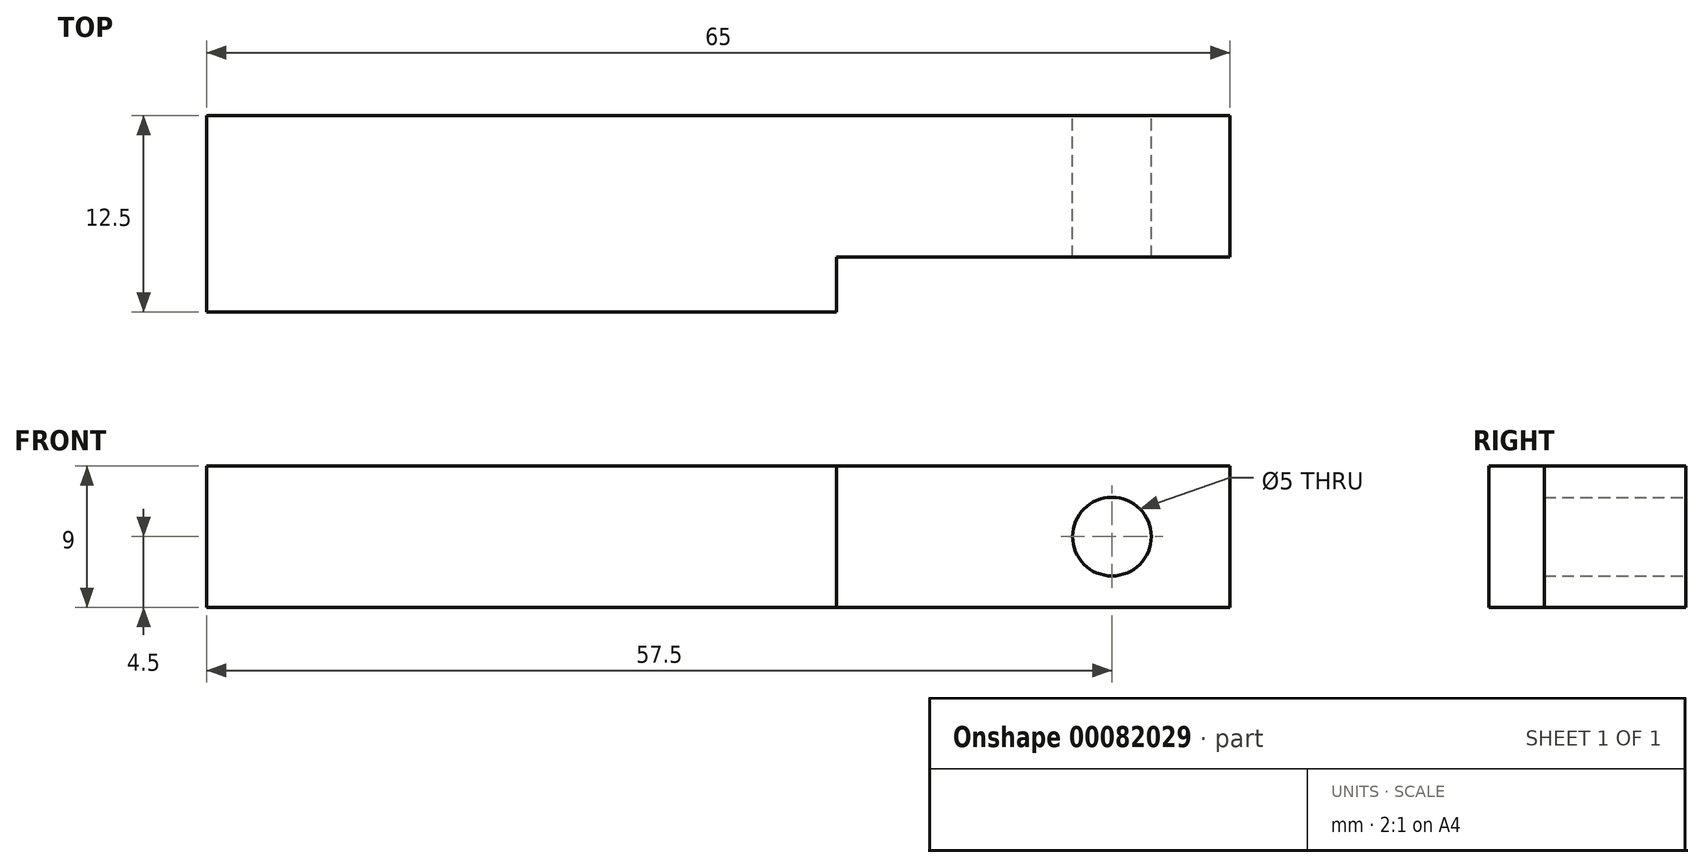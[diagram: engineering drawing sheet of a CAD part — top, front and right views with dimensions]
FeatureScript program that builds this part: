
annotation { "Feature Type Name" : "Feature", "Feature Type Description" : "" }
export const myFeature = defineFeature(function(context is Context, id is Id, definition is map)
    precondition{}
    {
        {
            var Q0;
            Q0=qCreatedBy(makeId("Front.planeOp"),FACE);
            var sketch = newSketch(context, id + "F0", { "sketchPlane" : qUnion([Q0])});
            skLineSegment(sketch, "E0.bottom", {"start": v(0, 0) * mm, "end": v(-65, 0) * mm});
            skLineSegment(sketch, "E0.top", {"start": v(0, 9) * mm, "end": v(-65, 9) * mm});
            skLineSegment(sketch, "E0.left", {"start": v(0, 0) * mm, "end": v(0, 9) * mm});
            skLineSegment(sketch, "E0.right", {"start": v(-65, 0) * mm, "end": v(-65, 9) * mm});
            skLineSegment(sketch, "E1", {"start": v(-32.5, 9) * mm, "end": v(-32.5, 0) * mm, "construction": true});
            skCircle(sketch, "E2", {"center": v(-57.5, 4.5) * mm, "radius": 2.5 * mm});
            skLineSegment(sketch, "E3", {"start": v(-65, 4.5) * mm, "end": v(0, 4.5) * mm, "construction": true});
            skCircle(sketch, "E4.MirrorC", {"center": v(-7.5, 4.5) * mm, "radius": 2.5 * mm});
            skSolve(sketch);
        }
        {
            var Q0;
            Q0=makeQuery(id+"F0.imprint","IMPRINT",FACE,{"disambiguationData":[TD([[makeQuery(id+"F0.imprint","IMPRINT",EDGE,{"derivedFrom":sQuery(id+"F0.wireOp",EDGE,"E0.bottom")}),-1.0]])]});
            extrude(context, id + "F1", {"entities" : qUnion([Q0]), "depth" : 9 * mm});
        }
        {
            var Q0;
            Q0=makeQuery(id+"F0.imprint","IMPRINT",FACE,{"disambiguationData":[TD([[makeQuery(id+"F0.imprint","IMPRINT",EDGE,{"derivedFrom":sQuery(id+"F0.wireOp",EDGE,"E2")}),1.0]])]});
            var Q1;
            Q1=makeQuery(id+"F0.imprint","IMPRINT",FACE,{"disambiguationData":[TD([[makeQuery(id+"F0.imprint","IMPRINT",EDGE,{"derivedFrom":sQuery(id+"F0.wireOp",EDGE,"E4.MirrorC")}),-1.0]])]});
            extrude(context, id + "F2", {"entities" : qUnion([Q0, Q1]), "operationType" : NewBodyOperationType.ADD, "depth" : 12.5 * mm});
        }
        {
            var Q0;
            Q0=makeQuery(id+"F1.opExtrude","SWEPT_FACE",FACE,{"disambiguationData":[OSD([sQuery(id+"F0.wireOp",EDGE,"E0.left")])]});
            var sketch = newSketch(context, id + "F3", { "sketchPlane" : qUnion([Q0])});
            skLineSegment(sketch, "E5.0", {"start": v(-9, 0) * mm, "end": v(-9, 9) * mm});
            skLineSegment(sketch, "E5.1", {"start": v(-9, 9) * mm, "end": v(0, 9) * mm});
            skLineSegment(sketch, "E5.2", {"start": v(-9, 0) * mm, "end": v(0, 0) * mm});
            skPoint(sketch, "E5.3", {"position": v(0, 4.5) * mm});
            skLineSegment(sketch, "E5.4", {"start": v(0, 0) * mm, "end": v(0, 9) * mm});
            skLineSegment(sketch, "E6", {"start": v(-9, 9) * mm, "end": v(-16.78, 9) * mm});
            skLineSegment(sketch, "E7", {"start": v(-16.78, 9) * mm, "end": v(-16.78, 0) * mm});
            skLineSegment(sketch, "E8", {"start": v(-16.78, 0) * mm, "end": v(-9, 0) * mm});
            skSolve(sketch);
        }
        {
            var Q0;
            Q0=makeQuery(id+"F3.imprint","IMPRINT",FACE,{"disambiguationData":[TD([[makeQuery(id+"F3.imprint","IMPRINT",EDGE,{"derivedFrom":sQuery(id+"F3.wireOp",EDGE,"E5.0")}),1.0]])]});
            extrude(context, id + "F4", {"entities" : qUnion([Q0]), "operationType" : NewBodyOperationType.REMOVE, "oppositeDirection" : true, "depth" : 25 * mm});
        }
    });
